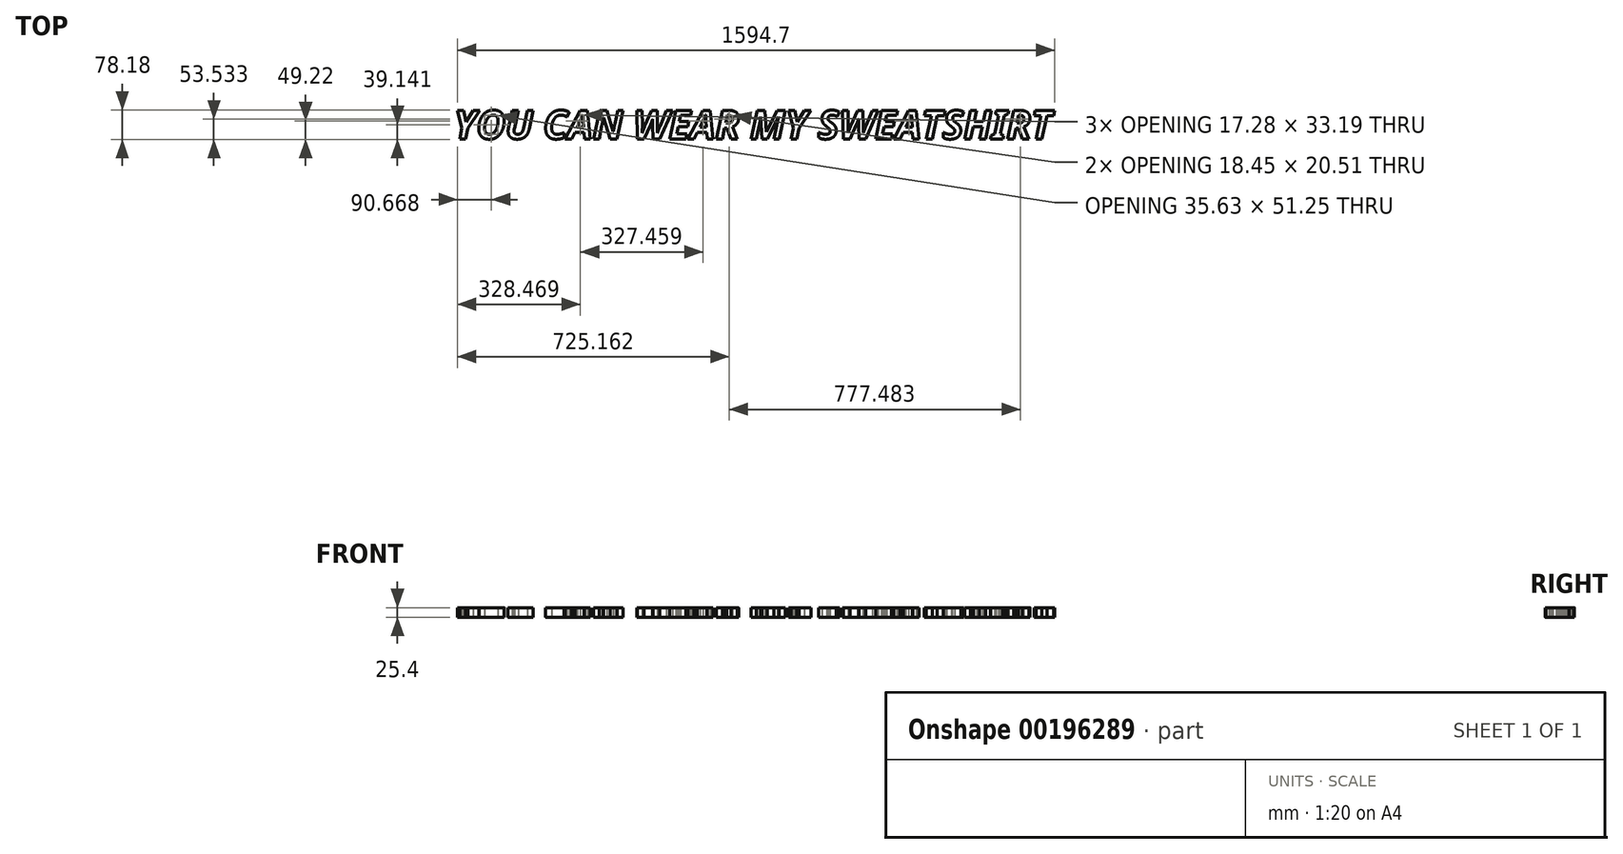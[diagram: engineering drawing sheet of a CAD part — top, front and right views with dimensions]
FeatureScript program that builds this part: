
annotation { "Feature Type Name" : "Feature", "Feature Type Description" : "" }
export const myFeature = defineFeature(function(context is Context, id is Id, definition is map)
    precondition{}
    {
        {
            var Q0;
            Q0=qCreatedBy(makeId("Top.planeOp"),FACE);
            var sketch = newSketch(context, id + "F0", { "sketchPlane" : qUnion([Q0])});
            skText(sketch, "E0", { "text": "YOU CAN WEAR MY SWEATSHIRT\n", "fontName": "NotoSans-BoldItalic.ttf"});
            const initialGuessF0  = {"E0": [-0.7742, -0.40905, 1, 0, 0.07658]};
            skSetInitialGuess(sketch, initialGuessF0);
            skSolve(sketch);
        }
        {
            var Q0;
            Q0=makeQuery(id+"F0.imprint","IMPRINT",FACE,{"disambiguationData":[TD([[makeQuery(id+"F0.imprint","IMPRINT",EDGE,{"derivedFrom":sQuery(id+"F0.wireOp",EDGE,"E0.sketch_text.stroke-0")}),-1.0]])]});
            var Q1;
            Q1=makeQuery(id+"F0.imprint","IMPRINT",FACE,{"disambiguationData":[TD([[makeQuery(id+"F0.imprint","IMPRINT",EDGE,{"derivedFrom":sQuery(id+"F0.wireOp",EDGE,"E0.sketch_text.stroke-29")}),-1.0]])]});
            var Q2;
            Q2=makeQuery(id+"F0.imprint","IMPRINT",FACE,{"disambiguationData":[TD([[makeQuery(id+"F0.imprint","IMPRINT",EDGE,{"derivedFrom":sQuery(id+"F0.wireOp",EDGE,"E0.sketch_text.stroke-44")}),-1.0]])]});
            var Q3;
            Q3=makeQuery(id+"F0.imprint","IMPRINT",FACE,{"disambiguationData":[TD([[makeQuery(id+"F0.imprint","IMPRINT",EDGE,{"derivedFrom":sQuery(id+"F0.wireOp",EDGE,"E0.sketch_text.stroke-77")}),-1.0]])]});
            var Q4;
            Q4=makeQuery(id+"F0.imprint","IMPRINT",FACE,{"disambiguationData":[TD([[makeQuery(id+"F0.imprint","IMPRINT",EDGE,{"derivedFrom":sQuery(id+"F0.wireOp",EDGE,"E0.sketch_text.stroke-92")}),-1.0]])]});
            var Q5;
            Q5=makeQuery(id+"F0.imprint","IMPRINT",FACE,{"disambiguationData":[TD([[makeQuery(id+"F0.imprint","IMPRINT",EDGE,{"derivedFrom":sQuery(id+"F0.wireOp",EDGE,"E0.sketch_text.stroke-117")}),-1.0]])]});
            var Q6;
            Q6=makeQuery(id+"F0.imprint","IMPRINT",FACE,{"disambiguationData":[TD([[makeQuery(id+"F0.imprint","IMPRINT",EDGE,{"derivedFrom":sQuery(id+"F0.wireOp",EDGE,"E0.sketch_text.stroke-163")}),-1.0]])]});
            var Q7;
            Q7=makeQuery(id+"F0.imprint","IMPRINT",FACE,{"disambiguationData":[TD([[makeQuery(id+"F0.imprint","IMPRINT",EDGE,{"derivedFrom":sQuery(id+"F0.wireOp",EDGE,"E0.sketch_text.stroke-181")}),-1.0]])]});
            var Q8;
            Q8=makeQuery(id+"F0.imprint","IMPRINT",FACE,{"disambiguationData":[TD([[makeQuery(id+"F0.imprint","IMPRINT",EDGE,{"derivedFrom":sQuery(id+"F0.wireOp",EDGE,"E0.sketch_text.stroke-190")}),-1.0]])]});
            var Q9;
            Q9=makeQuery(id+"F0.imprint","IMPRINT",FACE,{"disambiguationData":[TD([[makeQuery(id+"F0.imprint","IMPRINT",EDGE,{"derivedFrom":sQuery(id+"F0.wireOp",EDGE,"E0.sketch_text.stroke-214")}),-1.0]])]});
            var Q10;
            Q10=makeQuery(id+"F0.imprint","IMPRINT",FACE,{"disambiguationData":[TD([[makeQuery(id+"F0.imprint","IMPRINT",EDGE,{"derivedFrom":sQuery(id+"F0.wireOp",EDGE,"E0.sketch_text.stroke-239")}),-1.0]])]});
            var Q11;
            Q11=makeQuery(id+"F0.imprint","IMPRINT",FACE,{"disambiguationData":[TD([[makeQuery(id+"F0.imprint","IMPRINT",EDGE,{"derivedFrom":sQuery(id+"F0.wireOp",EDGE,"E0.sketch_text.stroke-266")}),-1.0]])]});
            var Q12;
            Q12=makeQuery(id+"F0.imprint","IMPRINT",FACE,{"disambiguationData":[TD([[makeQuery(id+"F0.imprint","IMPRINT",EDGE,{"derivedFrom":sQuery(id+"F0.wireOp",EDGE,"E0.sketch_text.stroke-274")}),-1.0]])]});
            var Q13;
            Q13=makeQuery(id+"F0.imprint","IMPRINT",FACE,{"disambiguationData":[TD([[makeQuery(id+"F0.imprint","IMPRINT",EDGE,{"derivedFrom":sQuery(id+"F0.wireOp",EDGE,"E0.sketch_text.stroke-298")}),-1.0]])]});
            var Q14;
            Q14=makeQuery(id+"F0.imprint","IMPRINT",FACE,{"disambiguationData":[TD([[makeQuery(id+"F0.imprint","IMPRINT",EDGE,{"derivedFrom":sQuery(id+"F0.wireOp",EDGE,"E0.sketch_text.stroke-310")}),-1.0]])]});
            var Q15;
            Q15=makeQuery(id+"F0.imprint","IMPRINT",FACE,{"disambiguationData":[TD([[makeQuery(id+"F0.imprint","IMPRINT",EDGE,{"derivedFrom":sQuery(id+"F0.wireOp",EDGE,"E0.sketch_text.stroke-341")}),-1.0]])]});
            var Q16;
            Q16=makeQuery(id+"F0.imprint","IMPRINT",FACE,{"disambiguationData":[TD([[makeQuery(id+"F0.imprint","IMPRINT",EDGE,{"derivedFrom":sQuery(id+"F0.wireOp",EDGE,"E0.sketch_text.stroke-9")}),-1.0]])]});
            var Q17;
            Q17=makeQuery(id+"F0.imprint","IMPRINT",FACE,{"disambiguationData":[TD([[makeQuery(id+"F0.imprint","IMPRINT",EDGE,{"derivedFrom":sQuery(id+"F0.wireOp",EDGE,"E0.sketch_text.stroke-62")}),-1.0]])]});
            var Q18;
            Q18=makeQuery(id+"F0.imprint","IMPRINT",FACE,{"disambiguationData":[TD([[makeQuery(id+"F0.imprint","IMPRINT",EDGE,{"derivedFrom":sQuery(id+"F0.wireOp",EDGE,"E0.sketch_text.stroke-129")}),-1.0]])]});
            var Q19;
            Q19=makeQuery(id+"F0.imprint","IMPRINT",FACE,{"disambiguationData":[TD([[makeQuery(id+"F0.imprint","IMPRINT",EDGE,{"derivedFrom":sQuery(id+"F0.wireOp",EDGE,"E0.sketch_text.stroke-144")}),-1.0]])]});
            var Q20;
            Q20=makeQuery(id+"F0.imprint","IMPRINT",FACE,{"disambiguationData":[TD([[makeQuery(id+"F0.imprint","IMPRINT",EDGE,{"derivedFrom":sQuery(id+"F0.wireOp",EDGE,"E0.sketch_text.stroke-251")}),-1.0]])]});
            var Q21;
            Q21=makeQuery(id+"F0.imprint","IMPRINT",FACE,{"disambiguationData":[TD([[makeQuery(id+"F0.imprint","IMPRINT",EDGE,{"derivedFrom":sQuery(id+"F0.wireOp",EDGE,"E0.sketch_text.stroke-322")}),-1.0]])]});
            var Q22;
            Q22 = qSketchRegion(id + "F0", true);
            extrude(context, id + "F1", {"entities" : qUnion([Q0, Q1, Q2, Q3, Q4, Q5, Q6, Q7, Q8, Q9, Q10, Q11, Q12, Q13, Q14, Q15, Q16, Q17, Q18, Q19, Q20, Q21, Q22]), "depth" : 25.4 * mm});
        }
    });
